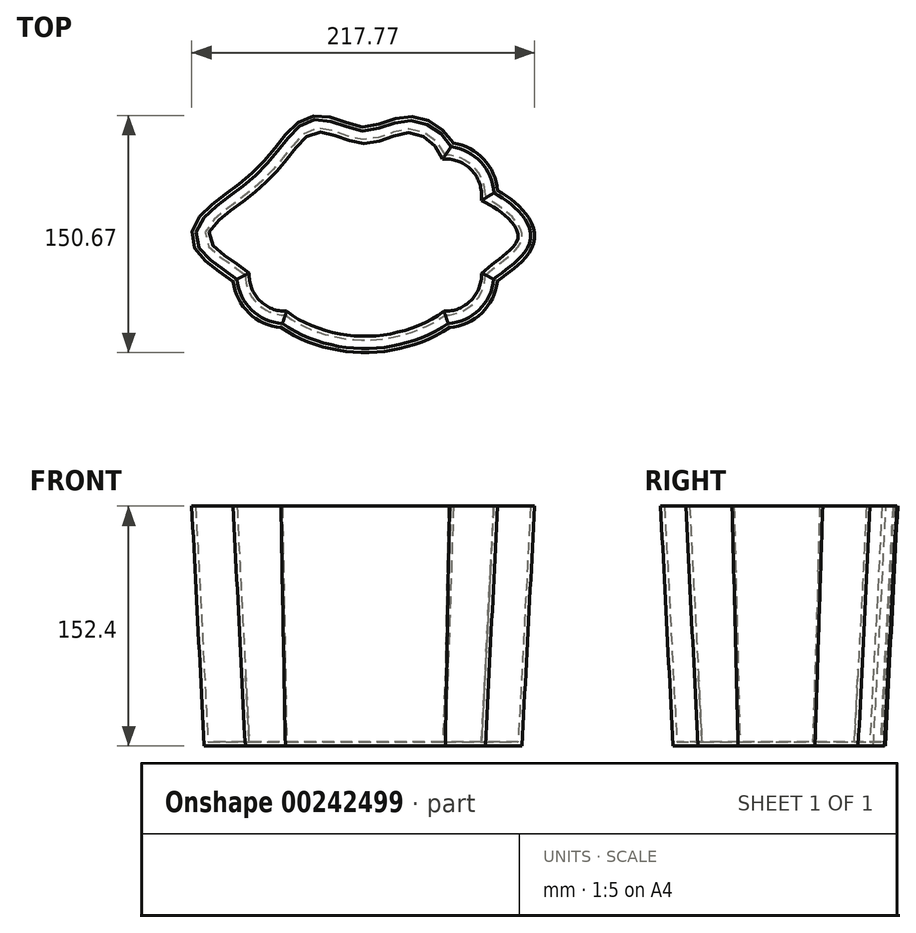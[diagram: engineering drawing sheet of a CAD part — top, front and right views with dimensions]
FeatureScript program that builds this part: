
annotation { "Feature Type Name" : "Feature", "Feature Type Description" : "" }
export const myFeature = defineFeature(function(context is Context, id is Id, definition is map)
    precondition{}
    {
        {
            var Q0;
            Q0=qCreatedBy(makeId("Top.planeOp"),FACE);
            var sketch = newSketch(context, id + "F0", { "sketchPlane" : qUnion([Q0])});
            skLineSegment(sketch, "E0.right", {"start": v(76.83, 24.54) * mm, "end": v(76.83, 26.58) * mm});
            skPoint(sketch, "E1.visualSharp", {"position": v(-75.57, 51.98) * mm});
            skPoint(sketch, "E2.visualSharp", {"position": v(76.83, 51.98) * mm});
            skArc(sketch, "E2.filletArc", {"start": v(76.75, 24.58) * mm, "mid": v(70.08, 43.82) * mm, "end": v(51.43, 51.98) * mm});
            skPoint(sketch, "E3.visualSharp", {"position": v(76.83, -49.62) * mm});
            skArc(sketch, "E3.filletArc", {"start": v(51.43, -49.62) * mm, "mid": v(69.39, -42.18) * mm, "end": v(76.83, -24.22) * mm});
            skPoint(sketch, "E4.visualSharp", {"position": v(-75.57, -49.62) * mm});
            skArc(sketch, "E4.filletArc", {"start": v(-75.57, -24.22) * mm, "mid": v(-68.13, -42.18) * mm, "end": v(-50.17, -49.62) * mm});
            skArc(sketch, "E5.filletArc", {"start": v(76.83, 26.58) * mm, "mid": v(69.39, 44.54) * mm, "end": v(51.43, 51.98) * mm});
            skFitSpline(sketch, "E6", {"points": [v(-75.57, 26.58) * mm, v(-101.64, 0) * mm, v(-75.57, -24.22) * mm, v(-50.17, -49.62) * mm, v(0, -65.54) * mm, v(51.43, -49.62) * mm, v(76.83, -24.22) * mm, v(100.13, 0) * mm, v(76.75, 24.58) * mm, v(54.87, 34.9) * mm, v(51.43, 51.98) * mm, v(30.05, 68.48) * mm, v(0, 61.77) * mm, v(-30.4, 69.07) * mm, v(-50.17, 51.98) * mm, v(-75.57, 26.58) * mm]});
            skSolve(sketch);
        }
        {
            var Q0;
            Q0 = qSketchRegion(id + "F0", true);
            extrude(context, id + "F1", {"entities" : qUnion([Q0]), "depth" : 152.4 * mm, "hasDraft" : true, "draftAngle" : 3 * degree});
        }
        {
            var Q0;
            Q0=makeQuery(id+"F1.opExtrude","CAP_FACE",FACE,{"disambiguationData":[OSD([sQuery(id+"F0.wireOp",EDGE,"E0.right"),sQuery(id+"F0.wireOp",EDGE,"E3.filletArc"),sQuery(id+"F0.wireOp",EDGE,"E4.filletArc"),sQuery(id+"F0.wireOp",EDGE,"E5.filletArc"),sQuery(id+"F0.wireOp",EDGE,"E6"),sQuery(id+"F0.wireOp",EDGE,"E6"),sQuery(id+"F0.wireOp",EDGE,"E6")])],"isStart":false});
            shell(context, id + "F2", {"entities" : qUnion([Q0]), "thickness" : 2.54 * mm});
        }
    });
